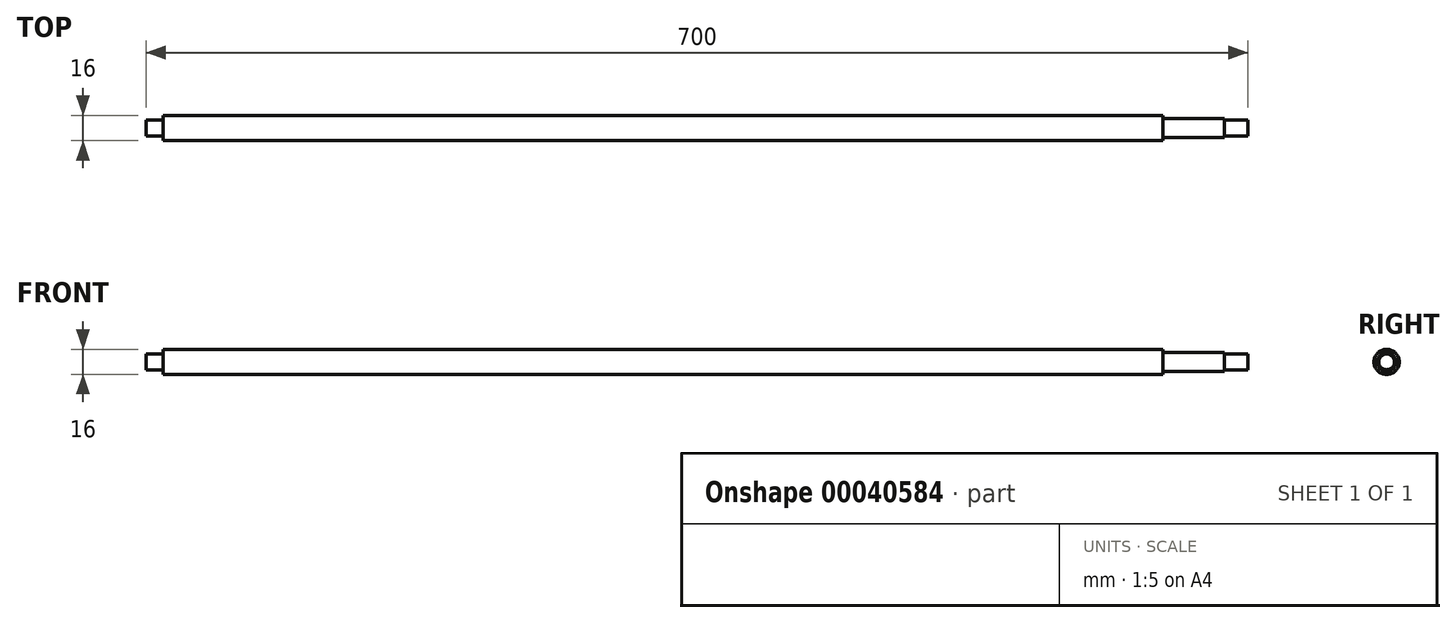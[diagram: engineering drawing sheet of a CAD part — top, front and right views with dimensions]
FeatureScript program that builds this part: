
annotation { "Feature Type Name" : "Feature", "Feature Type Description" : "" }
export const myFeature = defineFeature(function(context is Context, id is Id, definition is map)
    precondition{}
    {
        {
            var Q0;
            Q0=qCreatedBy(makeId("Top.planeOp"),FACE);
            var sketch = newSketch(context, id + "F0", { "sketchPlane" : qUnion([Q0])});
            skLineSegment(sketch, "E0", {"start": v(-350.57, -40.96) * mm, "end": v(349.43, -40.96) * mm});
            skLineSegment(sketch, "E1", {"start": v(-350.57, -40.96) * mm, "end": v(-350.57, -35.96) * mm});
            skLineSegment(sketch, "E2", {"start": v(-350.57, -35.96) * mm, "end": v(-339.57, -35.96) * mm});
            skLineSegment(sketch, "E3", {"start": v(-339.57, -35.96) * mm, "end": v(-339.57, -32.96) * mm});
            skLineSegment(sketch, "E4", {"start": v(-339.57, -32.96) * mm, "end": v(295.43, -32.96) * mm});
            skLineSegment(sketch, "E5", {"start": v(295.43, -32.96) * mm, "end": v(295.43, -34.96) * mm});
            skLineSegment(sketch, "E6", {"start": v(295.43, -34.96) * mm, "end": v(334.43, -34.96) * mm});
            skLineSegment(sketch, "E7", {"start": v(334.43, -34.96) * mm, "end": v(334.43, -35.96) * mm});
            skLineSegment(sketch, "E8", {"start": v(334.43, -35.96) * mm, "end": v(349.43, -35.96) * mm});
            skLineSegment(sketch, "E9", {"start": v(349.43, -35.96) * mm, "end": v(349.43, -40.96) * mm});
            skSolve(sketch);
        }
        {
            var Q0;
            Q0=makeQuery(id+"F0.imprint","IMPRINT",FACE,{"disambiguationData":[TD([[makeQuery(id+"F0.imprint","IMPRINT",EDGE,{"derivedFrom":sQuery(id+"F0.wireOp",EDGE,"E0")}),1.0]])]});
            var Q1;
            Q1=sQuery(id+"F0.wireOp",EDGE,"E0");
            revolve(context, id + "F1", {"entities" : qUnion([Q0]), "axis" : qUnion([Q1]), "revolveType" : RevolveType.FULL});
        }
    });
